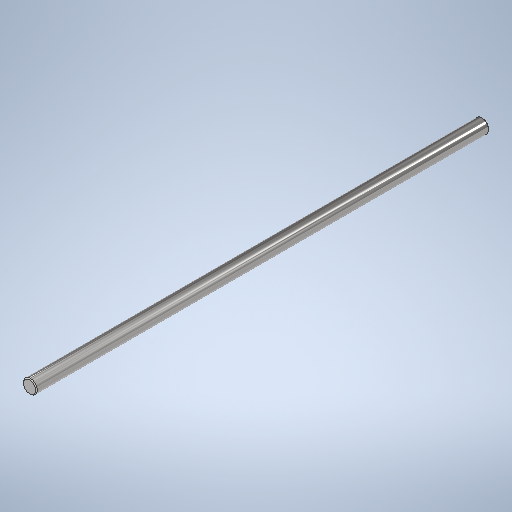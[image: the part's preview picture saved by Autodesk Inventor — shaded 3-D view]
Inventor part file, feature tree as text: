
AUTODESK INVENTOR PART (.ipt)
format: ipt  version: 2025.2 (Build 292293000, 293)  size: 259,072 bytes
history: native  units: mm
features: extrude x1, chamfer x1, sketch x1
ambient origin geometry x8: Origin, YZ Plane, XZ Plane, XY Plane, X Axis, Y Axis, Z Axis, Center Point
bodies: Solid1 (feature_tree)
feature tree (3):
  extrude  "Extrusion1"  Depth=264.0mm TaperAngle=0.0deg
  chamfer  "Chamfer1"  Distance=0.5mm Angle=45.0deg
  sketch  "Sketch1"  dims[d0=8.0mm d1=264.0mm d2=0.0mm d3=0.5mm d4=2.0mm d5=45.0deg]
